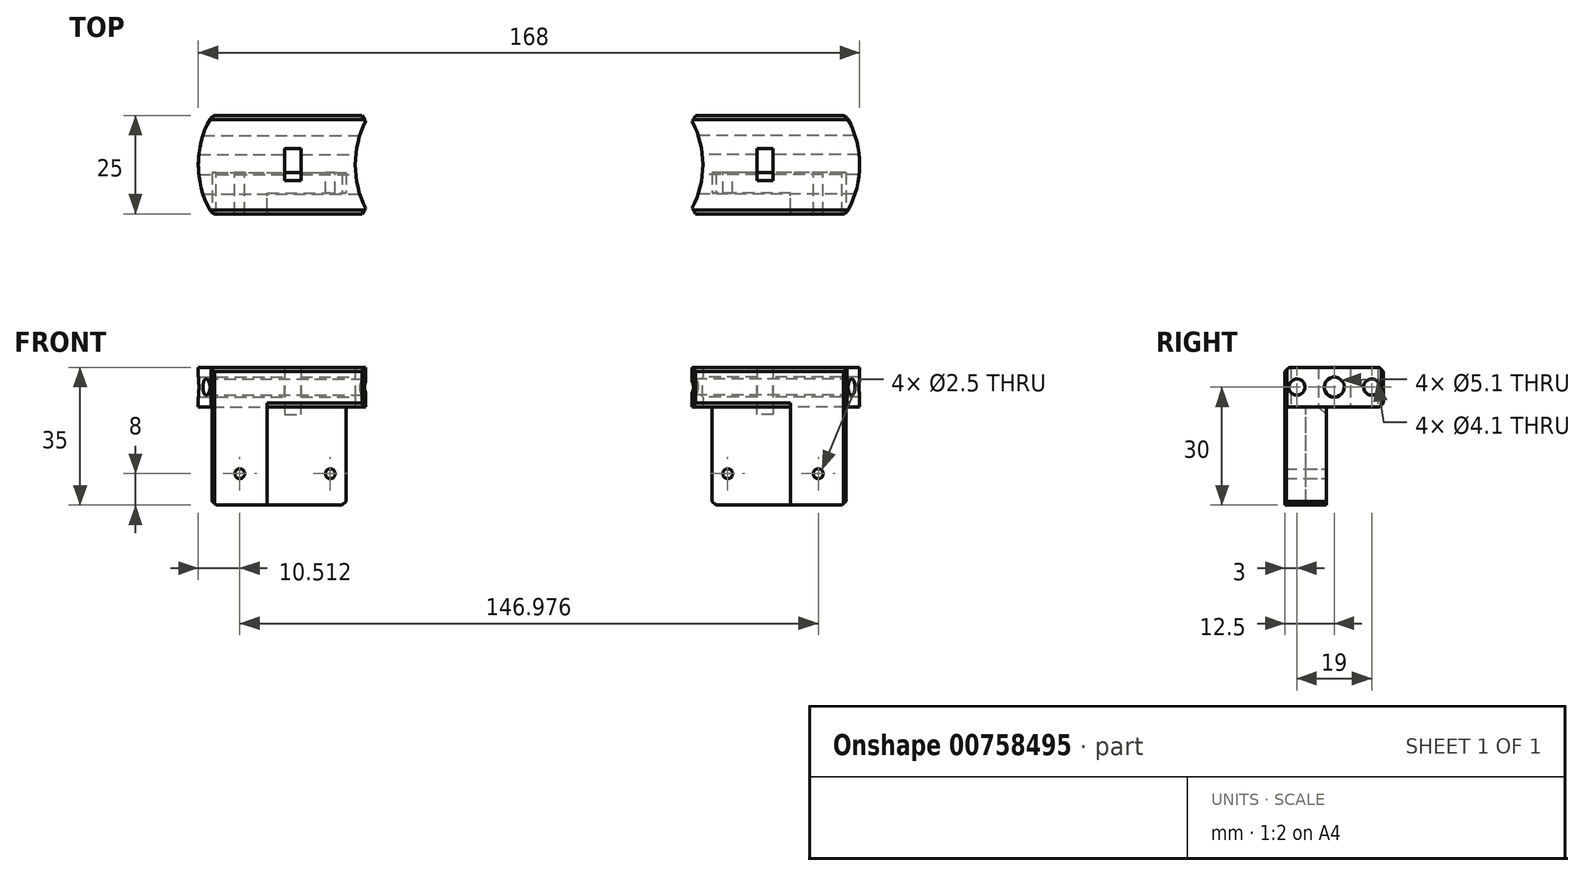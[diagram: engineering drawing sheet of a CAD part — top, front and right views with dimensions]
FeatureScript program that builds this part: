
annotation { "Feature Type Name" : "Feature", "Feature Type Description" : "" }
export const myFeature = defineFeature(function(context is Context, id is Id, definition is map)
    precondition{}
    {
        {
            var Q0;
            Q0=qCreatedBy(makeId("Top.planeOp"),FACE);
            var sketch = newSketch(context, id + "F0", { "sketchPlane" : qUnion([Q0])});
            skCircle(sketch, "E0", {"center": v(0, 0) * mm, "radius": 24 * mm});
            skLineSegment(sketch, "E1.bottom", {"start": v(20.49, 12.5) * mm, "end": v(-20.49, 12.5) * mm});
            skLineSegment(sketch, "E1.top", {"start": v(20.49, -12.5) * mm, "end": v(-20.49, -12.5) * mm});
            skLineSegment(sketch, "E1.left", {"start": v(20.49, 12.5) * mm, "end": v(20.49, -12.5) * mm});
            skLineSegment(sketch, "E1.right", {"start": v(-20.49, 12.5) * mm, "end": v(-20.49, -12.5) * mm});
            skLineSegment(sketch, "E2.bottom", {"start": v(2.05, 4.05) * mm, "end": v(-2.05, 4.05) * mm});
            skLineSegment(sketch, "E2.top", {"start": v(2.05, -4.05) * mm, "end": v(-2.05, -4.05) * mm});
            skLineSegment(sketch, "E2.left", {"start": v(2.05, 4.05) * mm, "end": v(2.05, -4.05) * mm});
            skLineSegment(sketch, "E2.right", {"start": v(-2.05, 4.05) * mm, "end": v(-2.05, -4.05) * mm});
            skCircle(sketch, "E3", {"center": v(39.85, 0) * mm, "radius": 24 * mm});
            skLineSegment(sketch, "E4", {"start": v(-20.49, -2) * mm, "end": v(13.51, -2) * mm});
            skLineSegment(sketch, "E5", {"start": v(13.51, -2) * mm, "end": v(13.51, -12.5) * mm});
            skLineSegment(sketch, "E6", {"start": v(-6.49, -12.5) * mm, "end": v(-6.49, -7.25) * mm});
            skLineSegment(sketch, "E7", {"start": v(-6.49, -7.25) * mm, "end": v(13.51, -7.25) * mm});
            skSolve(sketch);
        }
        {
            var Q0;
            {var subQ0=sQuery(id+"F0.wireOp",EDGE,"E1.right");Q0=makeQuery(id+"F0.imprint","IMPRINT",FACE,{"disambiguationData":[TD([[makeQuery(id+"F0.imprint","IMPRINT",EDGE,{"derivedFrom":subQ0}),-1.0]])]});}
            var Q1;
            {var subQ0=sQuery(id+"F0.wireOp",EDGE,"E1.right");Q1=makeQuery(id+"F0.imprint","IMPRINT",FACE,{"disambiguationData":[TD([[makeQuery(id+"F0.imprint","IMPRINT",EDGE,{"derivedFrom":subQ0}),1.0]])]});}
            var Q2;
            Q2=makeQuery(id+"F0.imprint","IMPRINT",FACE,{"disambiguationData":[TD([[makeQuery(id+"F0.imprint","IMPRINT",EDGE,{"derivedFrom":sQuery(id+"F0.wireOp",EDGE,"j2K1zlM2-5mF2-7mnx-XZQx-q8SdQ0DQluRe.bottom")}),-1.0]])]});
            var Q3;
            Q3=makeQuery(id+"F0.imprint","IMPRINT",FACE,{"disambiguationData":[TD([[makeQuery(id+"F0.imprint","IMPRINT",EDGE,{"derivedFrom":sQuery(id+"F0.wireOp",EDGE,"E2.bottom")}),-1.0]])]});
            var Q4;
            {var subQ3=sQuery(id+"F0.wireOp",EDGE,"E6");Q4=makeQuery(id+"F0.imprint","IMPRINT",FACE,{"disambiguationData":[TD([[makeQuery(id+"F0.imprint","IMPRINT",EDGE,{"derivedFrom":subQ3}),-1.0]])]});}
            extrude(context, id + "F1", {"entities" : qUnion([Q0, Q1, Q2, Q3, Q4]), "depth" : 10 * mm, "offsetDistance" : 25 * mm});
        }
        {
            var Q0;
            {var subQ1=sQuery(id+"F0.wireOp",EDGE,"E2.top");Q0=makeQuery(id+"F0.imprint","IMPRINT",FACE,{"disambiguationData":[TD([[makeQuery(id+"F0.imprint","IMPRINT",EDGE,{"derivedFrom":subQ1}),1.0]])]});}
            var Q1;
            {var subQ0=sQuery(id+"F0.wireOp",EDGE,"E2.top");Q1=makeQuery(id+"F0.imprint","IMPRINT",FACE,{"disambiguationData":[TD([[makeQuery(id+"F0.imprint","IMPRINT",EDGE,{"derivedFrom":subQ0}),-1.0]])]});}
            extrude(context, id + "F2", {"entities" : qUnion([Q0, Q1]), "operationType" : NewBodyOperationType.ADD, "oppositeDirection" : true, "depth" : 25 * mm, "offsetDistance" : 25 * mm});
        }
        {
            var Q0;
            Q0=qCreatedBy(makeId("Right.planeOp"),FACE);
            cPlane(context, id + "F3", {"entities" : qUnion([Q0]), "cplaneType" : CPlaneType.OFFSET, "offset" : 30 * mm, "width" : 150 * mm, "height" : 150 * mm});
        }
        {
            var Q0;
            Q0=qCreatedBy(id+"F3.planeOp",FACE);
            var sketch = newSketch(context, id + "F4", { "sketchPlane" : qUnion([Q0])});
            skPoint(sketch, "E8", {"position": v(0, 5) * mm});
            skPoint(sketch, "E9", {"position": v(9.5, 5) * mm});
            skPoint(sketch, "E10.MirrorP", {"position": v(-9.5, 5) * mm});
            skSolve(sketch);
        }
        {
            var Q0;
            Q0=sQuery(id+"F4.wireOp",VERTEX,"E8");
            var Q1;
            Q1=makeQuery(id+"F1.opExtrude","SWEPT_BODY",BODY,{"disambiguationData":[OSD([sQuery(id+"F0.wireOp",EDGE,"E0"),sQuery(id+"F0.wireOp",EDGE,"E1.bottom"),sQuery(id+"F0.wireOp",EDGE,"E1.top"),sQuery(id+"F0.wireOp",EDGE,"E2.bottom"),sQuery(id+"F0.wireOp",EDGE,"E2.top"),sQuery(id+"F0.wireOp",EDGE,"E2.left"),sQuery(id+"F0.wireOp",EDGE,"E2.right"),sQuery(id+"F0.wireOp",EDGE,"j2K1zlM2-5mF2-7mnx-XZQx-q8SdQ0DQluRe.bottom"),sQuery(id+"F0.wireOp",EDGE,"j2K1zlM2-5mF2-7mnx-XZQx-q8SdQ0DQluRe.top")])]});
            hole(context, id + "F5", {"style" : HoleStyle.SIMPLE, "endStyle" : HoleEndStyle.THROUGH, "holeDiameter" : 5.1 * mm, "majorDiameter" : 5 * mm, "isTappedThrough" : true, "tappedDepth" : 12 * mm, "tapClearance" : 3, "locations" : qUnion([Q0]), "scope" : qUnion([Q1])});
        }
        {
            var Q0;
            Q0=sQuery(id+"F4.wireOp",VERTEX,"E10.MirrorP");
            var Q1;
            Q1=sQuery(id+"F4.wireOp",VERTEX,"E9");
            var Q2;
            Q2=makeQuery(id+"F1.opExtrude","SWEPT_BODY",BODY,{"disambiguationData":[OSD([sQuery(id+"F0.wireOp",EDGE,"E0"),sQuery(id+"F0.wireOp",EDGE,"E1.bottom"),sQuery(id+"F0.wireOp",EDGE,"E1.top"),sQuery(id+"F0.wireOp",EDGE,"E2.bottom"),sQuery(id+"F0.wireOp",EDGE,"E2.top"),sQuery(id+"F0.wireOp",EDGE,"E2.left"),sQuery(id+"F0.wireOp",EDGE,"E2.right"),sQuery(id+"F0.wireOp",EDGE,"j2K1zlM2-5mF2-7mnx-XZQx-q8SdQ0DQluRe.bottom"),sQuery(id+"F0.wireOp",EDGE,"j2K1zlM2-5mF2-7mnx-XZQx-q8SdQ0DQluRe.top")])]});
            hole(context, id + "F6", {"style" : HoleStyle.SIMPLE, "endStyle" : HoleEndStyle.THROUGH, "holeDiameter" : 4.1 * mm, "majorDiameter" : 5 * mm, "isTappedThrough" : true, "tappedDepth" : 12 * mm, "tapClearance" : 3, "locations" : qUnion([Q0, Q1]), "scope" : qUnion([Q2])});
        }
        {
            var Q0;
            Q0=makeQuery(id+"F2.opExtrude","SWEPT_FACE",FACE,{"disambiguationData":[OSD([sQuery(id+"F0.wireOp",EDGE,"E4")])]});
            var sketch = newSketch(context, id + "F7", { "sketchPlane" : qUnion([Q0])});
            skPoint(sketch, "E11", {"position": v(-9.51, -17) * mm});
            skPoint(sketch, "E12", {"position": v(13.49, -17) * mm});
            skSolve(sketch);
        }
        {
            var Q0;
            Q0=sQuery(id+"F7.wireOp",VERTEX,"E11");
            var Q1;
            Q1=sQuery(id+"F7.wireOp",VERTEX,"E12");
            var Q2;
            Q2=makeQuery(id+"F1.opExtrude","SWEPT_BODY",BODY,{"disambiguationData":[OSD([sQuery(id+"F0.wireOp",EDGE,"E0"),sQuery(id+"F0.wireOp",EDGE,"E1.bottom"),sQuery(id+"F0.wireOp",EDGE,"E1.top"),sQuery(id+"F0.wireOp",EDGE,"E2.bottom"),sQuery(id+"F0.wireOp",EDGE,"E2.top"),sQuery(id+"F0.wireOp",EDGE,"E2.left"),sQuery(id+"F0.wireOp",EDGE,"E2.right"),sQuery(id+"F0.wireOp",EDGE,"E3")])]});
            hole(context, id + "F8", {"style" : HoleStyle.SIMPLE, "endStyle" : HoleEndStyle.THROUGH, "holeDiameter" : 2.5 * mm, "majorDiameter" : 5 * mm, "isTappedThrough" : true, "tappedDepth" : 12 * mm, "tapClearance" : 3, "locations" : qUnion([Q0, Q1]), "scope" : qUnion([Q2])});
        }
        {
            var Q0;
            {var subQ0=sQuery(id+"F0.wireOp",EDGE,"E4");Q0=makeQuery(id+"F2.boolean.opBoolean","SPLIT",EDGE,{"disambiguationData":[topologyDisambiguationEdgeConnected([makeQuery(id+"F2.opExtrude","CAP_FACE",FACE,{"disambiguationData":[OSD([sQuery(id+"F0.wireOp",EDGE,"E1.top"),sQuery(id+"F0.wireOp",EDGE,"E1.right"),subQ0,sQuery(id+"F0.wireOp",EDGE,"E5"),sQuery(id+"F0.wireOp",EDGE,"E6"),sQuery(id+"F0.wireOp",EDGE,"E7")])],"isStart":true}),makeQuery(id+"F2.opExtrude","SWEPT_FACE",FACE,{"disambiguationData":[OSD([subQ0])]})])],"derivedFrom":makeQuery(id+"F2.opExtrude","CAP_EDGE",EDGE,{"disambiguationData":[OSD([subQ0])],"isStart":true})});}
            chamfer(context, id + "F9", {"entities" : qUnion([Q0]), "width" : 2 * mm, "tangentPropagation" : true});
        }
        {
            var Q0;
            Q0=makeQuery(id+"F1.opExtrude","SWEPT_FACE",FACE,{"disambiguationData":[OSD([sQuery(id+"F0.wireOp",EDGE,"E1.bottom")])]});
            var Q1;
            Q1=makeQuery(id+"F1.opExtrude","CAP_EDGE",EDGE,{"disambiguationData":[OSD([sQuery(id+"F0.wireOp",EDGE,"E1.top")])],"isStart":false});
            var Q2;
            Q2=makeQuery(id+"F1.opExtrude","CAP_EDGE",EDGE,{"disambiguationData":[OSD([sQuery(id+"F0.wireOp",EDGE,"E1.top")])],"isStart":true});
            var Q3;
            Q3=makeQuery(id+"F1.opExtrude","SWEPT_EDGE",EDGE,{"disambiguationData":[OSD([sQuery(id+"F0.wireOp",EDGE,"E1.top"),sQuery(id+"F0.wireOp",EDGE,"E3")])]});
            var Q4;
            Q4=makeQuery(id+"F1.opExtrude","SWEPT_EDGE",EDGE,{"disambiguationData":[OSD([sQuery(id+"F0.wireOp",EDGE,"E0"),sQuery(id+"F0.wireOp",EDGE,"E1.top"),sQuery(id+"F0.wireOp",EDGE,"E1.right")])]});
            var Q5;
            Q5=makeQuery(id+"F2.opExtrude","CAP_EDGE",EDGE,{"disambiguationData":[OSD([sQuery(id+"F0.wireOp",EDGE,"E5")])],"isStart":true});
            var Q6;
            Q6=makeQuery(id+"F2.opExtrude","CAP_EDGE",EDGE,{"disambiguationData":[OSD([sQuery(id+"F0.wireOp",EDGE,"E1.right")])],"isStart":true});
            var Q7;
            Q7=makeQuery(id+"F2.opExtrude","CAP_EDGE",EDGE,{"disambiguationData":[OSD([sQuery(id+"F0.wireOp",EDGE,"E5")])],"isStart":false});
            var Q8;
            Q8=makeQuery(id+"F2.opExtrude","CAP_EDGE",EDGE,{"disambiguationData":[OSD([sQuery(id+"F0.wireOp",EDGE,"E1.right")])],"isStart":false});
            chamfer(context, id + "F10", {"entities" : qUnion([Q0, Q1, Q2, Q3, Q4, Q5, Q6, Q7, Q8]), "width" : 1 * mm, "tangentPropagation" : true});
        }
        {
            var Q0;
            Q0=qCreatedBy(makeId("Right.planeOp"),FACE);
            cPlane(context, id + "F11", {"entities" : qUnion([Q0]), "cplaneType" : CPlaneType.OFFSET, "offset" : 60 * mm, "width" : 150 * mm, "height" : 150 * mm});
        }
        {
            var Q0;
            Q0=makeQuery(id+"F1.opExtrude","SWEPT_BODY",BODY,{"disambiguationData":[OSD([sQuery(id+"F0.wireOp",EDGE,"E0"),sQuery(id+"F0.wireOp",EDGE,"E1.bottom"),sQuery(id+"F0.wireOp",EDGE,"E1.top"),sQuery(id+"F0.wireOp",EDGE,"E2.bottom"),sQuery(id+"F0.wireOp",EDGE,"E2.top"),sQuery(id+"F0.wireOp",EDGE,"E2.left"),sQuery(id+"F0.wireOp",EDGE,"E2.right"),sQuery(id+"F0.wireOp",EDGE,"E3")])]});
            var Q1;
            Q1=qCreatedBy(id+"F11.planeOp",FACE);
            mirror(context, id + "F12", {"entities" : qUnion([Q0]), "mirrorPlane" : qUnion([Q1])});
        }
    });
